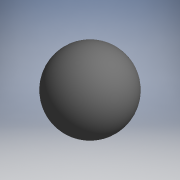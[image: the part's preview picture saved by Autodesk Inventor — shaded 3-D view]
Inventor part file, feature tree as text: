
AUTODESK INVENTOR PART (.ipt)
format: ipt  version: 2017.3 (Build 213256000, 256)  size: 111,616 bytes
history: native  units: mm (DEFAULTED — no unit token found)
features: other x7, revolve x1, sketch x1
ambient origin geometry x8: Origin, YZ Plane, XZ Plane, XY Plane, X Axis, Y Axis, Z Axis, Center Point
bodies: Solid1 (feature_tree)
feature tree (9):
  revolve  "Revolution1"  [1 undecoded]
  other  "ip_st_1_XY"
  other  "ip_st_1_YZ"
  other  "ip_st_1_ZX"
  other  "ip_st_1_X"
  other  "ip_st_1_Y"
  other  "ip_st_1_Z"
  other  "ip_st_1_Center"
  sketch  "Sketch_1"  dims[d0=360.0deg]
note: 1 required parameter value undecoded (feature->parameter linkage not recoverable at this tier; creation-order binding heuristic only, values carry confidence <= 0.55)
